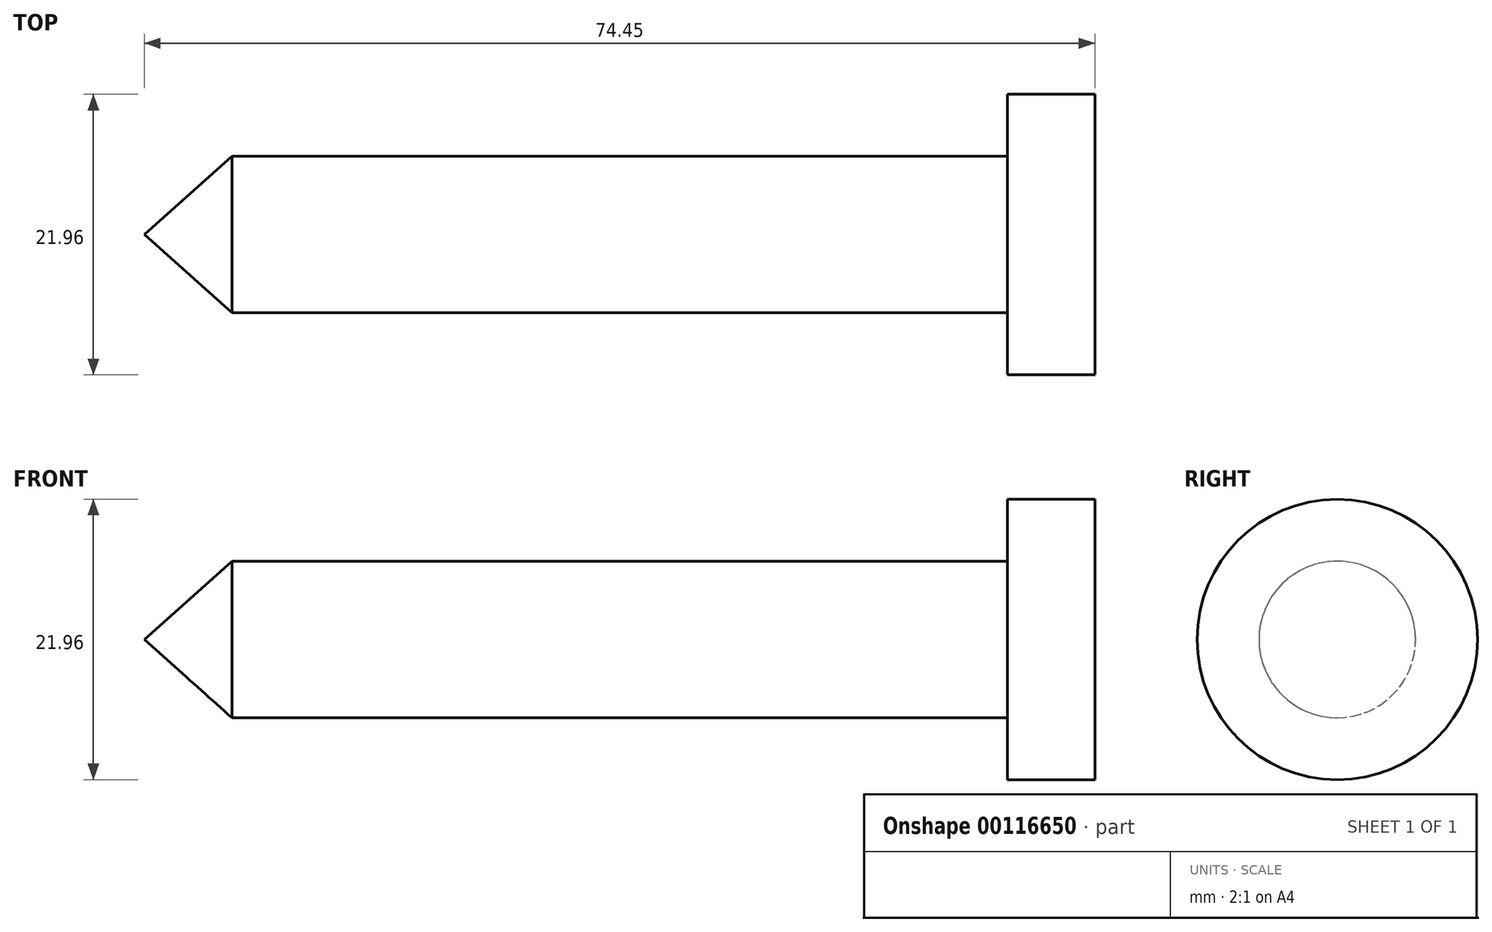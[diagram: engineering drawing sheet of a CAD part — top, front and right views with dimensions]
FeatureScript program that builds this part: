
annotation { "Feature Type Name" : "Feature", "Feature Type Description" : "" }
export const myFeature = defineFeature(function(context is Context, id is Id, definition is map)
    precondition{}
    {
        {
            var Q0;
            Q0=qCreatedBy(makeId("Front.planeOp"),FACE);
            var sketch = newSketch(context, id + "F0", { "sketchPlane" : qUnion([Q0])});
            skLineSegment(sketch, "E0.bottom", {"start": v(-33.94, 6.13) * mm, "end": v(26.81, 6.13) * mm});
            skLineSegment(sketch, "E0.top", {"start": v(-33.94, 0) * mm, "end": v(26.81, 0) * mm});
            skLineSegment(sketch, "E0.left", {"start": v(-33.94, 6.13) * mm, "end": v(-33.94, 0) * mm});
            skLineSegment(sketch, "E0.right", {"start": v(26.81, 6.13) * mm, "end": v(26.81, 0) * mm});
            skLineSegment(sketch, "E1.bottom", {"start": v(26.81, 10.98) * mm, "end": v(33.66, 10.98) * mm});
            skLineSegment(sketch, "E1.top", {"start": v(26.81, 0) * mm, "end": v(33.66, 0) * mm});
            skLineSegment(sketch, "E1.left", {"start": v(26.81, 10.98) * mm, "end": v(26.81, 0) * mm});
            skLineSegment(sketch, "E1.right", {"start": v(33.66, 10.98) * mm, "end": v(33.66, 0) * mm});
            skLineSegment(sketch, "E2", {"start": v(-33.94, 6.13) * mm, "end": v(-40.79, 0) * mm});
            skLineSegment(sketch, "E3", {"start": v(-33.94, 0) * mm, "end": v(-40.79, 0) * mm});
            skSolve(sketch);
        }
        {
            var Q0;
            Q0 = qSketchRegion(id + "F0", true);
            var Q1;
            Q1=sQuery(id+"F0.wireOp",EDGE,"E0.top");
            revolve(context, id + "F1", {"entities" : qUnion([Q0]), "axis" : qUnion([Q1]), "revolveType" : RevolveType.FULL});
        }
    });
